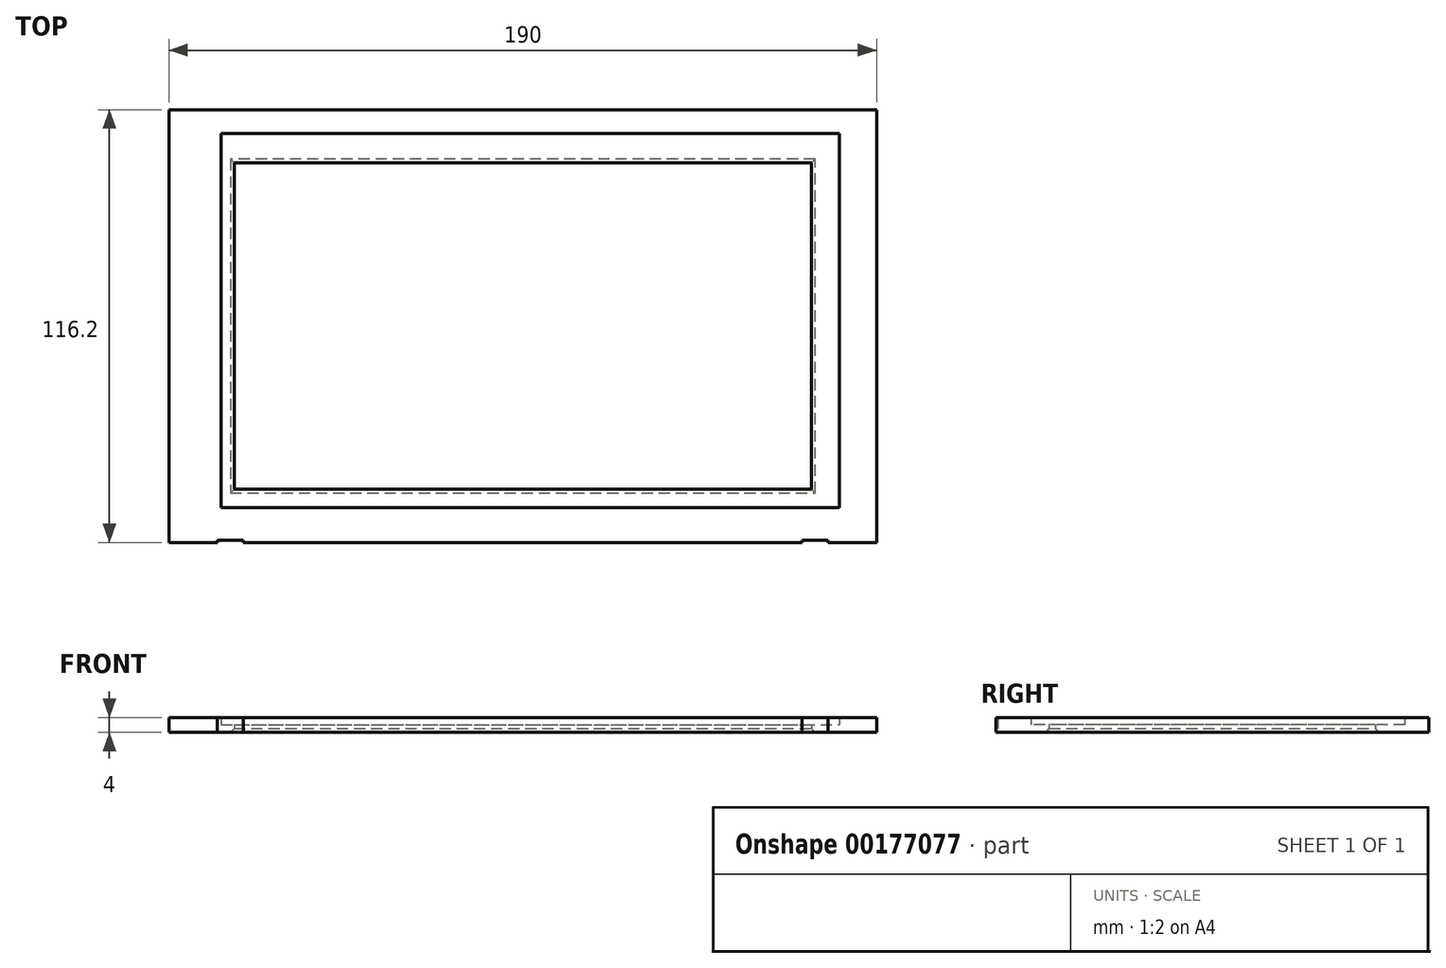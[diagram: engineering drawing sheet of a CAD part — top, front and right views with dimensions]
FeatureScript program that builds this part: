
annotation { "Feature Type Name" : "Feature", "Feature Type Description" : "" }
export const myFeature = defineFeature(function(context is Context, id is Id, definition is map)
    precondition{}
    {
        {
            var Q0;
            Q0=qCreatedBy(makeId("Top.planeOp"),FACE);
            var sketch = newSketch(context, id + "F0", { "sketchPlane" : qUnion([Q0])});
            skLineSegment(sketch, "E0.bottom", {"start": v(-92.01, 48.91) * mm, "end": v(97.99, 48.91) * mm});
            skLineSegment(sketch, "E0.top", {"start": v(-92.01, -67.29) * mm, "end": v(97.99, -67.29) * mm});
            skLineSegment(sketch, "E0.left", {"start": v(-92.01, 48.91) * mm, "end": v(-92.01, -67.29) * mm});
            skLineSegment(sketch, "E0.right", {"start": v(97.99, 48.91) * mm, "end": v(97.99, -67.29) * mm});
            skLineSegment(sketch, "E1.bottom", {"start": v(-74.51, 34.61) * mm, "end": v(80.49, 34.61) * mm});
            skLineSegment(sketch, "E1.top", {"start": v(-74.51, -52.99) * mm, "end": v(80.49, -52.99) * mm});
            skLineSegment(sketch, "E1.left", {"start": v(-74.51, 34.61) * mm, "end": v(-74.51, -52.99) * mm});
            skLineSegment(sketch, "E1.right", {"start": v(80.49, 34.61) * mm, "end": v(80.49, -52.99) * mm});
            skLineSegment(sketch, "E2.bottom", {"start": v(-78.01, 42.51) * mm, "end": v(87.99, 42.51) * mm});
            skLineSegment(sketch, "E2.top", {"start": v(-78.01, -57.89) * mm, "end": v(87.99, -57.89) * mm});
            skLineSegment(sketch, "E2.left", {"start": v(-78.01, 42.51) * mm, "end": v(-78.01, -57.89) * mm});
            skLineSegment(sketch, "E2.right", {"start": v(87.99, 42.51) * mm, "end": v(87.99, -57.89) * mm});
            skLineSegment(sketch, "E3.bottom", {"start": v(84.99, -67.29) * mm, "end": v(77.99, -67.29) * mm});
            skLineSegment(sketch, "E3.top", {"start": v(84.99, -66.74) * mm, "end": v(77.99, -66.74) * mm});
            skLineSegment(sketch, "E3.left", {"start": v(84.99, -67.29) * mm, "end": v(84.99, -66.74) * mm});
            skLineSegment(sketch, "E3.right", {"start": v(77.99, -67.29) * mm, "end": v(77.99, -66.74) * mm});
            skLineSegment(sketch, "E4", {"start": v(2.99, -67.29) * mm, "end": v(2.99, -38.45) * mm, "construction": true});
            skPoint(sketch, "E4.endSnap0", {"position": v(2.99, -52.99) * mm});
            skLineSegment(sketch, "E5.MirrorCS", {"start": v(-79.01, -66.74) * mm, "end": v(-72.01, -66.74) * mm});
            skLineSegment(sketch, "E6.MirrorCS", {"start": v(-72.01, -67.29) * mm, "end": v(-72.01, -66.74) * mm});
            skLineSegment(sketch, "E7.MirrorCS", {"start": v(-79.01, -67.29) * mm, "end": v(-79.01, -66.74) * mm});
            skSolve(sketch);
        }
        {
            var Q0;
            Q0=makeQuery(id+"F0.imprint","IMPRINT",FACE,{"disambiguationData":[TD([[makeQuery(id+"F0.imprint","IMPRINT",EDGE,{"derivedFrom":sQuery(id+"F0.wireOp",EDGE,"E0.bottom")}),-1.0]])]});
            extrude(context, id + "F1", {"entities" : qUnion([Q0]), "depth" : 4 * mm});
        }
        {
            var Q0;
            Q0=makeQuery(id+"F0.imprint","IMPRINT",FACE,{"disambiguationData":[TD([[makeQuery(id+"F0.imprint","IMPRINT",EDGE,{"derivedFrom":sQuery(id+"F0.wireOp",EDGE,"E1.bottom")}),1.0]])]});
            extrude(context, id + "F2", {"entities" : qUnion([Q0]), "operationType" : NewBodyOperationType.ADD, "depth" : 2 * mm});
        }
        {
            var Q0;
            Q0=makeQuery(id+"F2.opExtrude","CAP_EDGE",EDGE,{"disambiguationData":[OSD([sQuery(id+"F0.wireOp",EDGE,"E1.top")])],"isStart":true});
            var Q1;
            Q1=makeQuery(id+"F2.opExtrude","CAP_EDGE",EDGE,{"disambiguationData":[OSD([sQuery(id+"F0.wireOp",EDGE,"E1.left")])],"isStart":true});
            var Q2;
            Q2=makeQuery(id+"F2.opExtrude","CAP_EDGE",EDGE,{"disambiguationData":[OSD([sQuery(id+"F0.wireOp",EDGE,"E1.bottom")])],"isStart":true});
            var Q3;
            Q3=makeQuery(id+"F2.opExtrude","CAP_EDGE",EDGE,{"disambiguationData":[OSD([sQuery(id+"F0.wireOp",EDGE,"E1.right")])],"isStart":true});
            chamfer(context, id + "F3", {"entities" : qUnion([Q0, Q1, Q2, Q3]), "width" : 1 * mm, "tangentPropagation" : true});
        }
    });
